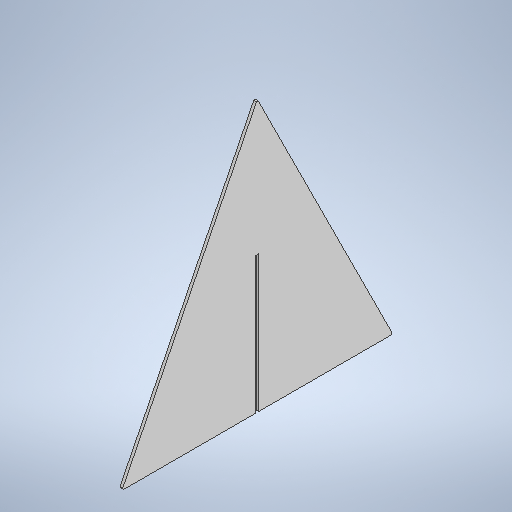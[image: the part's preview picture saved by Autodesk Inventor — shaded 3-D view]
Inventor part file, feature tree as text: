
AUTODESK INVENTOR PART (.ipt)
format: ipt  version: 2025 (Build 290162010, 162A)  size: 277,504 bytes
history: native  units: mm
features: other x5, sketch x2, sheet_metal_op x1, extrude x1
ambient origin geometry x8: Origin, YZ Plane, XZ Plane, XY Plane, X Axis, Y Axis, Z Axis, Center Point
bodies: Solid1 (feature_tree)
feature tree (9):
  other  "MSC 207 CONE BLADE"
  sheet_metal_op  "Face1"
  extrude  "Extrusion2"  Depth=300.0mm
  other  "Corner Chamfer1"
  other  "Corner Chamfer2"
  sketch  "Sketch1"  dims[d0=300.0mm d1=300.0mm]
  other  "Plate1"
  sketch  "Sketch3"  dims[d2=3.0mm d7=3.2mm d8=151.0mm d9=0.0mm d10=0.0mm d11=2.0mm d12=6.0mm d13=45.0deg d14=2.0mm d15=6.0mm d16=45.0deg]
  other  "Definition1"
